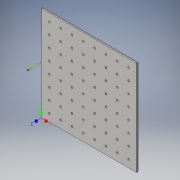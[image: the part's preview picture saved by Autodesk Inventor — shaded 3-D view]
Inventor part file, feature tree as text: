
AUTODESK INVENTOR PART (.ipt)
format: ipt  version: 2016 (Build 200138000, 138)  size: 212,992 bytes
history: native  units: in
note: dims shown in document units (in); Inventor stores cm internally (conversion verified against a paired STEP export)
features: extrude x2, sketch x2, pattern_linear x1
ambient origin geometry x8: Origin, YZ Plane, XZ Plane, XY Plane, X Axis, Y Axis, Z Axis, Center Point
bodies: Solid1 (feature_tree)
feature tree (5):
  extrude  "Extrusion1"  Depth=5.9055in
  extrude  "Extrusion2"  Depth=0.1181in
  pattern_linear  "Rectangular Pattern1"  Spacing1=0.4724in  [1 undecoded]
  sketch  "Sketch3"  dims[d0=5.9055in d1=5.9055in]
  sketch  "Sketch5"  dims[d2=0.1181in d3=0.0in d15=0.4724in d16=0.4724in d17=0.1181in d18=0.1181in d19=0.0in d20=3.1496in d22=0.7087in d23=3.1496in d25=0.7087in]
note: 1 required parameter value undecoded (feature->parameter linkage not recoverable at this tier; creation-order binding heuristic only, values carry confidence <= 0.55)
